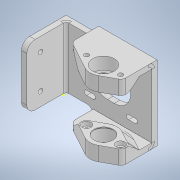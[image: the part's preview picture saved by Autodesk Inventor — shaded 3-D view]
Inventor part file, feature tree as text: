
AUTODESK INVENTOR PART (.ipt)
format: ipt  version: 2022 (Build 260153000, 153)  size: 676,352 bytes
history: native  units: in
note: dims shown in document units (in); Inventor stores cm internally (conversion verified against a paired STEP export)
features: projected_geometry x29, sketch x17, extrude x12, other x7, sheet_metal_op x7, move_body x3, hole x2, chamfer x2, fillet x2, mirror x2, plane x1, boolean_combine x1
ambient origin geometry x8: Origin, YZ Plane, XZ Plane, XY Plane, X Axis, Y Axis, Z Axis, Center Point
bodies: Solid3 (feature_tree), Solid2 (feature_tree)
feature tree (85):
  other  "Z Drive Bearing Holder.ipt"
  sheet_metal_op  "Face1"
  sheet_metal_op  "Flange2"
  sketch  "Sketch3"  dims[d1=2.1654in d4=1.2205in]
  hole  "Hole2"  [1 undecoded]
  sheet_metal_op  "Flange3"
  chamfer  "Corner Round2"
  hole  "Hole3"  [1 undecoded]
  extrude  "Extrusion3"  Depth=1.2205in
  extrude  "Extrusion4"  Depth=0.1969in
  extrude  "Extrusion5"  Depth=0.1969in
  extrude  "Extrusion7"  Depth=0.08in
  extrude  "Extrusion8"  Depth=0.08in
  extrude  "Extrusion9"  Depth=2.4803in
  extrude  "Extrusion10"  Depth=0.4921in
  fillet  "Fillet2"  Radius=1.6929in
  plane  "Work Plane2"
  mirror  "Mirror2"
  move_body  "Move Body2"
  move_body  "Move Body3"
  move_body  "Move Body8"
  boolean_combine  "Combine1"
  extrude  "Extrusion11"  Depth=0.5512in
  extrude  "Extrusion12"  Depth=0.04in
  extrude  "Extrusion15"  Depth=0.08in
  fillet  "Fillet3"  Radius=0.32in
  mirror  "Mirror3"
  extrude  "Extrusion13"  Depth=0.08in
  extrude  "Extrusion16"  Depth=0.3937in
  chamfer  "Chamfer1"  Distance=0.08in
  sketch  "Sketch22"  dims[d98=0.2362in d99=0.08in d100=0.04in d101=0.16in d102=0.08in d103=1.2205in d104=90.0deg d105=0.08in d106=0.32in d107=0.08in d108=0.08in d109=0.3937in d110=0.3937in d111=0.3937in d112=0.1339in d113=0.2362in d114=0.2559in d115=0.1181in d116=0.6181in d117=0.08in d118=0.8108in d119=0.3937in d120=0.0in d121=0.3937in d122=0.0in d123=0.1575in d124=0.3937in d125=0.0in d128=0.3937in d129=0.0in d130=0.0787in d131=0.0in d132=0.1575in d133=0.0787in d134=0.0in d135=0.3937in d136=0.0in d137=0.1969in d138=0.3937in d142=90.0deg d143=90.0deg d156=0.3937in d157=0.0in d158=0.3937in d159=0.0in d160=1.9907in d161=-0.8636in d162=-0.2362in d163=0.3937in d164=0.0in d167=0.4188in d168=0.0in d169=0.1969in d170=0.4188in d171=0.0in d172=0.2555in d173=0.0787in d174=45.0deg]
  other  "Plate1"
  sketch  "Sketch6"  dims[d7=1.2205in d8=1.2205in]
  other  "Plate4"
  sheet_metal_op  "Bend3"
  sheet_metal_op  "Corner2"
  sketch  "Sketch7"  dims[d9=1.2205in d10=1.2205in]
  other  "Plate5"
  sheet_metal_op  "Bend4"
  sheet_metal_op  "Corner3"
  sketch  "Sketch8"  dims[d11=0.0669in d12=0.1969in]
  sketch  "Sketch9"  dims[d13=0.4724in d14=0.1969in]
  projected_geometry  "Projected Loop2"
  projected_geometry  "Projected Loop3"
  sketch  "Sketch10"  dims[d15=0.5906in d16=0.08in]
  projected_geometry  "Projected Loop4"
  sketch  "Sketch11"  dims[d36=0.5512in d41=0.08in]
  projected_geometry  "Projected Loop5"
  projected_geometry  "Projected Loop6"
  projected_geometry  "Projected Loop7"
  projected_geometry  "Projected Loop8"
  sketch  "Sketch12"  dims[d42=0.0in]
  projected_geometry  "Projected Loop9"
  projected_geometry  "Projected Loop10"
  projected_geometry  "Projected Loop11"
  projected_geometry  "Projected Loop12"
  sketch  "Sketch13"  dims[d43=0.1339in d44=0.2362in d45=0.2559in d46=0.1181in d47=90.0deg d48=0.315in d49=0.8108in d53=2.4803in]
  projected_geometry  "Projected Loop13"
  sketch  "Sketch14"  dims[d55=0.4921in d56=0.4921in d83=1.6929in]
  projected_geometry  "Projected Loop14"
  projected_geometry  "Projected Loop15"
  projected_geometry  "Projected Loop16"
  projected_geometry  "Projected Loop17"
  sketch  "Sketch15"  dims[d84=0.1969in d85=0.5512in]
  projected_geometry  "Projected Loop18"
  projected_geometry  "Projected Loop19"
  projected_geometry  "Projected Loop20"
  projected_geometry  "Projected Loop21"
  projected_geometry  "Projected Loop22"
  other  "Solid1::Z Drive Bearing Holder.ipt"
  other  "TaggingFeature1"
  sketch  "Sketch16"  dims[d86=0.08in d87=0.04in]
  projected_geometry  "Projected Loop23"
  sketch  "Sketch17"  dims[d88=0.16in d89=0.08in]
  projected_geometry  "Projected Loop24"
  sketch  "Sketch18"  dims[d90=1.2205in d91=90.0deg d92=0.08in d93=0.32in]
  projected_geometry  "Projected Loop25"
  sketch  "Sketch20"  dims[d94=0.08in d95=0.08in]
  projected_geometry  "Projected Loop27"
  projected_geometry  "Projected Loop28"
  sketch  "Sketch21"  dims[d96=0.3937in d97=0.1575in]
  projected_geometry  "Projected Loop29"
  projected_geometry  "Projected Loop30"
  projected_geometry  "Projected Loop31"
  other  "Cut1"
note: 2 required parameter values undecoded (feature->parameter linkage not recoverable at this tier; creation-order binding heuristic only, values carry confidence <= 0.55)
